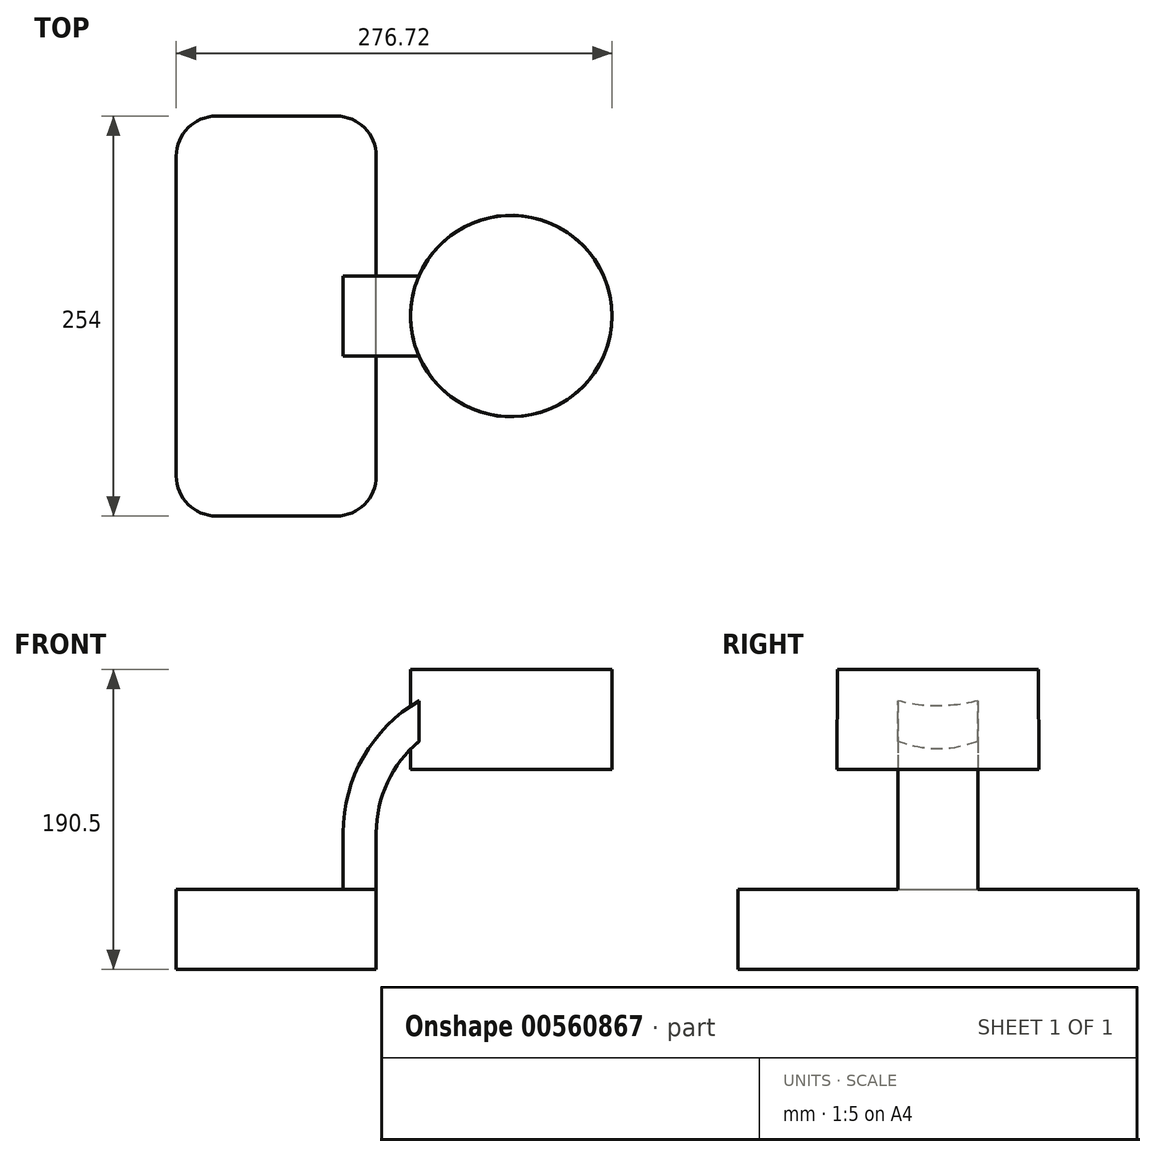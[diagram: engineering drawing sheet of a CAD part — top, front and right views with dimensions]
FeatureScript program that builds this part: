
annotation { "Feature Type Name" : "Feature", "Feature Type Description" : "" }
export const myFeature = defineFeature(function(context is Context, id is Id, definition is map)
    precondition{}
    {
        {
            var Q0;
            Q0=qCreatedBy(makeId("Front.planeOp"),FACE);
            var sketch = newSketch(context, id + "F0", { "sketchPlane" : qUnion([Q0])});
            skLineSegment(sketch, "E0.bottom", {"start": v(-63.5, 25.4) * mm, "end": v(63.5, 25.4) * mm});
            skLineSegment(sketch, "E0.top", {"start": v(-63.5, -25.4) * mm, "end": v(63.5, -25.4) * mm});
            skLineSegment(sketch, "E0.left", {"start": v(-63.5, 25.4) * mm, "end": v(-63.5, -25.4) * mm});
            skLineSegment(sketch, "E0.right", {"start": v(63.5, 25.4) * mm, "end": v(63.5, -25.4) * mm});
            skPoint(sketch, "E0.middle", {"position": v(0, 0) * mm});
            skLineSegment(sketch, "E1.bottom", {"start": v(149.22, 165.1) * mm, "end": v(231.77, 165.1) * mm});
            skLineSegment(sketch, "E1.top", {"start": v(149.22, 101.6) * mm, "end": v(231.77, 101.6) * mm});
            skLineSegment(sketch, "E1.left", {"start": v(149.22, 165.1) * mm, "end": v(149.22, 101.6) * mm});
            skLineSegment(sketch, "E1.right", {"start": v(231.77, 165.1) * mm, "end": v(231.77, 101.6) * mm});
            skPoint(sketch, "E1.middle", {"position": v(190.5, 133.35) * mm});
            skLineSegment(sketch, "E2", {"start": v(63.5, 25.4) * mm, "end": v(63.5, 61.25) * mm});
            skArc(sketch, "E3", {"start": v(63.5, 61.25) * mm, "mid": v(85.82, 115.13) * mm, "end": v(139.7, 137.45) * mm});
            skLineSegment(sketch, "E4", {"start": v(139.7, 137.45) * mm, "end": v(213.1, 137.45) * mm});
            skLineSegment(sketch, "E5.0", {"start": v(139.7, 158.5) * mm, "end": v(213.1, 158.5) * mm});
            skArc(sketch, "E5.1", {"start": v(42.44, 61.25) * mm, "mid": v(70.93, 130.02) * mm, "end": v(139.7, 158.5) * mm});
            skLineSegment(sketch, "E5.2", {"start": v(42.44, 25.4) * mm, "end": v(42.44, 61.25) * mm});
            skLineSegment(sketch, "E6", {"start": v(213.22, 101.6) * mm, "end": v(213.1, 165.1) * mm});
            skFitSpline(sketch, "E7", {"points": [v(-63.5, 25.4) * mm, v(139.7, 158.5) * mm], "startDerivative": vector(63.43, 248.18) * mm, "endDerivative": vector(232.6, -22.7) * mm});
            skSolve(sketch);
        }
        {
            var Q0;
            Q0=makeQuery(id+"F0.imprint","IMPRINT",FACE,{"disambiguationData":[TD([[makeQuery(id+"F0.imprint","IMPRINT",EDGE,{"derivedFrom":sQuery(id+"F0.wireOp",EDGE,"E0.top")}),1.0]])]});
            extrude(context, id + "F1", {"entities" : qUnion([Q0]), "endBound" : BoundingType.SYMMETRIC, "depth" : 254 * mm, "offsetDistance" : 25.4 * mm});
        }
        {
            var Q0;
            Q0=makeQuery(id+"F0.imprint","IMPRINT",FACE,{"disambiguationData":[TD([[makeQuery(id+"F0.imprint","IMPRINT",EDGE,{"derivedFrom":sQuery(id+"F0.wireOp",EDGE,"E5.1")}),1.0]])]});
            var Q1;
            {var subQ1=sQuery(id+"F0.wireOp",EDGE,"E2");Q1=makeQuery(id+"F0.imprint","IMPRINT",FACE,{"disambiguationData":[TD([[makeQuery(id+"F0.imprint","IMPRINT",EDGE,{"derivedFrom":subQ1}),1.0]])]});}
            extrude(context, id + "F2", {"entities" : qUnion([Q0, Q1]), "operationType" : NewBodyOperationType.ADD, "endBound" : BoundingType.SYMMETRIC, "depth" : 50.8 * mm, "offsetDistance" : 25.4 * mm});
        }
        {
            var Q0;
            {var subQ6=sQuery(id+"F0.wireOp",EDGE,"E6");Q0=makeQuery(id+"F0.imprint","IMPRINT",FACE,{"disambiguationData":[TD([[makeQuery(id+"F0.imprint","IMPRINT",EDGE,{"derivedFrom":subQ6}),1.0]])]});}
            var Q1;
            Q1=sQuery(id+"F0.wireOp",EDGE,"E1.left");
            revolve(context, id + "F3", {"operationType" : NewBodyOperationType.ADD, "entities" : qUnion([Q0]), "axis" : qUnion([Q1]), "revolveType" : RevolveType.FULL});
        }
        {
            var Q0;
            Q0=makeQuery(id+"F1.opExtrude","CAP_EDGE",EDGE,{"disambiguationData":[OSD([sQuery(id+"F0.wireOp",EDGE,"E0.right")])],"isStart":false});
            var Q1;
            Q1=makeQuery(id+"F1.opExtrude","CAP_EDGE",EDGE,{"disambiguationData":[OSD([sQuery(id+"F0.wireOp",EDGE,"E0.left")])],"isStart":false});
            var Q2;
            Q2=makeQuery(id+"F1.opExtrude","CAP_EDGE",EDGE,{"disambiguationData":[OSD([sQuery(id+"F0.wireOp",EDGE,"E0.right")])],"isStart":true});
            var Q3;
            Q3=makeQuery(id+"F1.opExtrude","CAP_EDGE",EDGE,{"disambiguationData":[OSD([sQuery(id+"F0.wireOp",EDGE,"E0.left")])],"isStart":true});
            fillet(context, id + "F4", {"entities" : qUnion([Q0, Q1, Q2, Q3]), "radius" : 25.4 * mm, "tangentPropagation" : true, "allowEdgeOverflow" : false});
        }
    });
